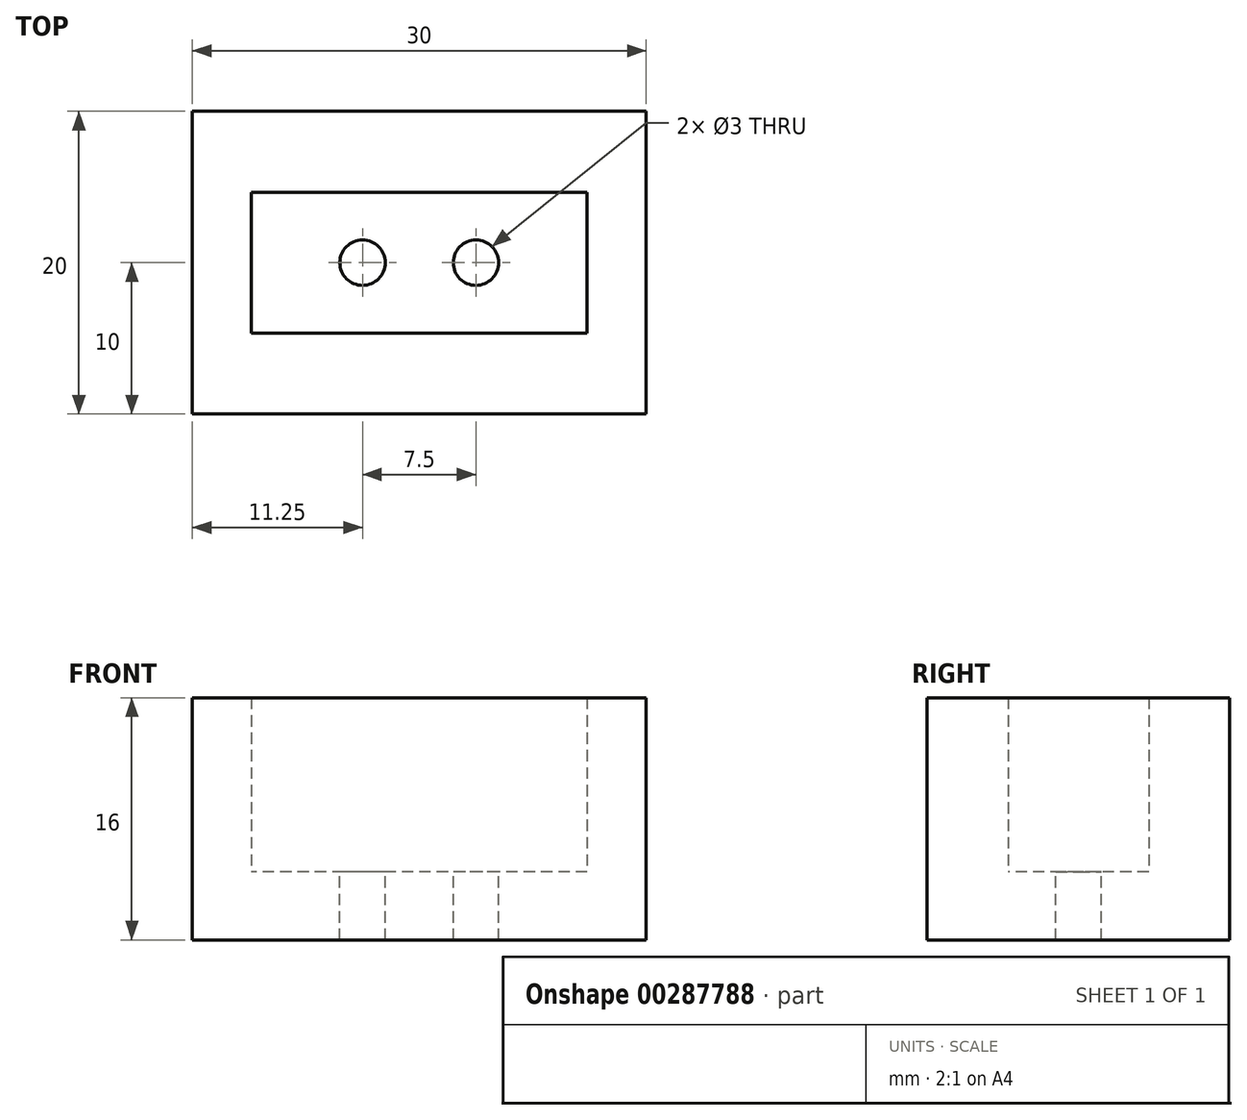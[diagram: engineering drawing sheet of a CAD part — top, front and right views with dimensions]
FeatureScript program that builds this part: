
annotation { "Feature Type Name" : "Feature", "Feature Type Description" : "" }
export const myFeature = defineFeature(function(context is Context, id is Id, definition is map)
    precondition{}
    {
        {
            var Q0;
            Q0=qCreatedBy(makeId("Top.planeOp"),FACE);
            var sketch = newSketch(context, id + "F0", { "sketchPlane" : qUnion([Q0])});
            skLineSegment(sketch, "E0.bottom", {"start": v(15, 10) * mm, "end": v(-15, 10) * mm});
            skLineSegment(sketch, "E0.top", {"start": v(15, -10) * mm, "end": v(-15, -10) * mm});
            skLineSegment(sketch, "E0.left", {"start": v(15, 10) * mm, "end": v(15, -10) * mm});
            skLineSegment(sketch, "E0.right", {"start": v(-15, 10) * mm, "end": v(-15, -10) * mm});
            skPoint(sketch, "E0.middle", {"position": v(0, 0) * mm});
            skLineSegment(sketch, "E1.bottom", {"start": v(11.1, 4.65) * mm, "end": v(-11.1, 4.65) * mm});
            skLineSegment(sketch, "E1.top", {"start": v(11.1, -4.65) * mm, "end": v(-11.1, -4.65) * mm});
            skLineSegment(sketch, "E1.left", {"start": v(11.1, 4.65) * mm, "end": v(11.1, -4.65) * mm});
            skLineSegment(sketch, "E1.right", {"start": v(-11.1, 4.65) * mm, "end": v(-11.1, -4.65) * mm});
            skSolve(sketch);
        }
        {
            var Q0;
            Q0 = qSketchRegion(id + "F0", true);
            extrude(context, id + "F1", {"entities" : qUnion([Q0]), "depth" : 11.5 * mm});
        }
        {
            var Q0;
            Q0=qCreatedBy(makeId("Top.planeOp"),FACE);
            var sketch = newSketch(context, id + "F2", { "sketchPlane" : qUnion([Q0])});
            skLineSegment(sketch, "E2.0", {"start": v(15, -10) * mm, "end": v(-15, -10) * mm});
            skLineSegment(sketch, "E3.0", {"start": v(15, 10) * mm, "end": v(15, -10) * mm});
            skLineSegment(sketch, "E4.0", {"start": v(15, 10) * mm, "end": v(-15, 10) * mm});
            skLineSegment(sketch, "E5.0", {"start": v(-15, 10) * mm, "end": v(-15, -10) * mm});
            skCircle(sketch, "E6", {"center": v(-3.75, 0) * mm, "radius": 1.5 * mm});
            skCircle(sketch, "E7", {"center": v(3.75, 0) * mm, "radius": 1.5 * mm});
            skSolve(sketch);
        }
        {
            var Q0;
            Q0 = qSketchRegion(id + "F2", true);
            extrude(context, id + "F3", {"entities" : qUnion([Q0]), "operationType" : NewBodyOperationType.ADD, "oppositeDirection" : true, "depth" : 4.5 * mm});
        }
    });
